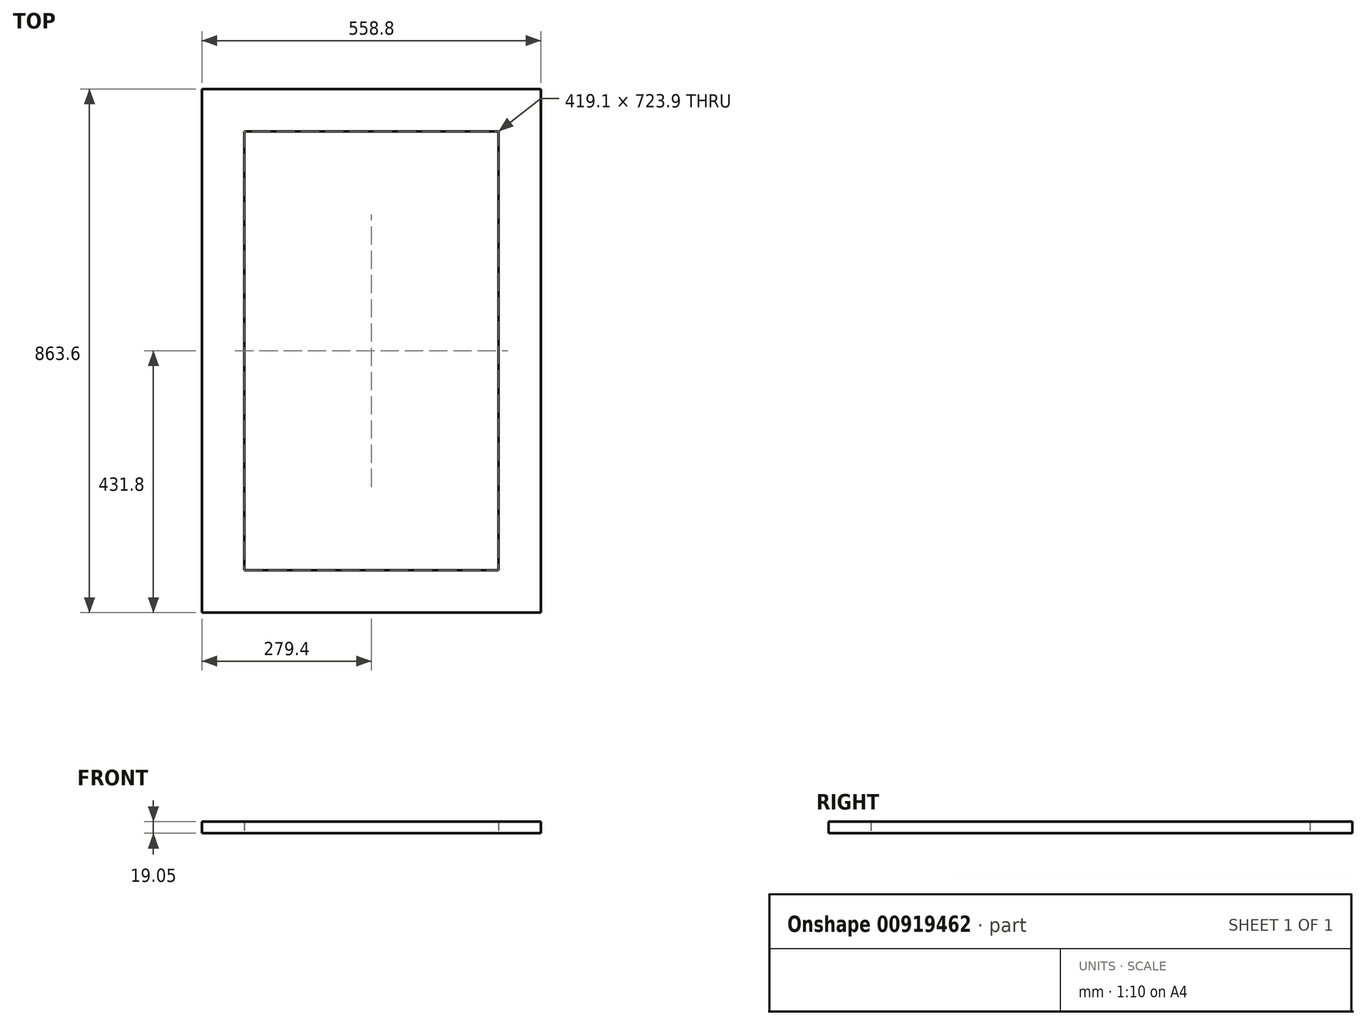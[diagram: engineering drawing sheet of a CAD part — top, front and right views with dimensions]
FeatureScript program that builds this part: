
annotation { "Feature Type Name" : "Feature", "Feature Type Description" : "" }
export const myFeature = defineFeature(function(context is Context, id is Id, definition is map)
    precondition{}
    {
        {
            var Q0;
            Q0=qCreatedBy(makeId("Top.planeOp"),FACE);
            var sketch = newSketch(context, id + "F0", { "sketchPlane" : qUnion([Q0])});
            skLineSegment(sketch, "E0.bottom", {"start": v(279.4, 431.8) * mm, "end": v(-279.4, 431.8) * mm});
            skLineSegment(sketch, "E0.top", {"start": v(279.4, -431.8) * mm, "end": v(-279.4, -431.8) * mm});
            skLineSegment(sketch, "E0.left", {"start": v(279.4, 431.8) * mm, "end": v(279.4, -431.8) * mm});
            skLineSegment(sketch, "E0.right", {"start": v(-279.4, 431.8) * mm, "end": v(-279.4, -431.8) * mm});
            skPoint(sketch, "E0.middle", {"position": v(0, 0) * mm});
            skLineSegment(sketch, "E1.bottom", {"start": v(209.55, 361.95) * mm, "end": v(-209.55, 361.95) * mm});
            skLineSegment(sketch, "E1.top", {"start": v(209.55, -361.95) * mm, "end": v(-209.55, -361.95) * mm});
            skLineSegment(sketch, "E1.left", {"start": v(209.55, 361.95) * mm, "end": v(209.55, -361.95) * mm});
            skLineSegment(sketch, "E1.right", {"start": v(-209.55, 361.95) * mm, "end": v(-209.55, -361.95) * mm});
            skSolve(sketch);
        }
        {
            var Q0;
            Q0=makeQuery(id+"F0.imprint","IMPRINT",FACE,{"disambiguationData":[TD([[makeQuery(id+"F0.imprint","IMPRINT",EDGE,{"derivedFrom":sQuery(id+"F0.wireOp",EDGE,"E0.bottom")}),1.0]])]});
            extrude(context, id + "F1", {"entities" : qUnion([Q0]), "depth" : 19.05 * mm, "offsetDistance" : 25.4 * mm});
        }
    });
